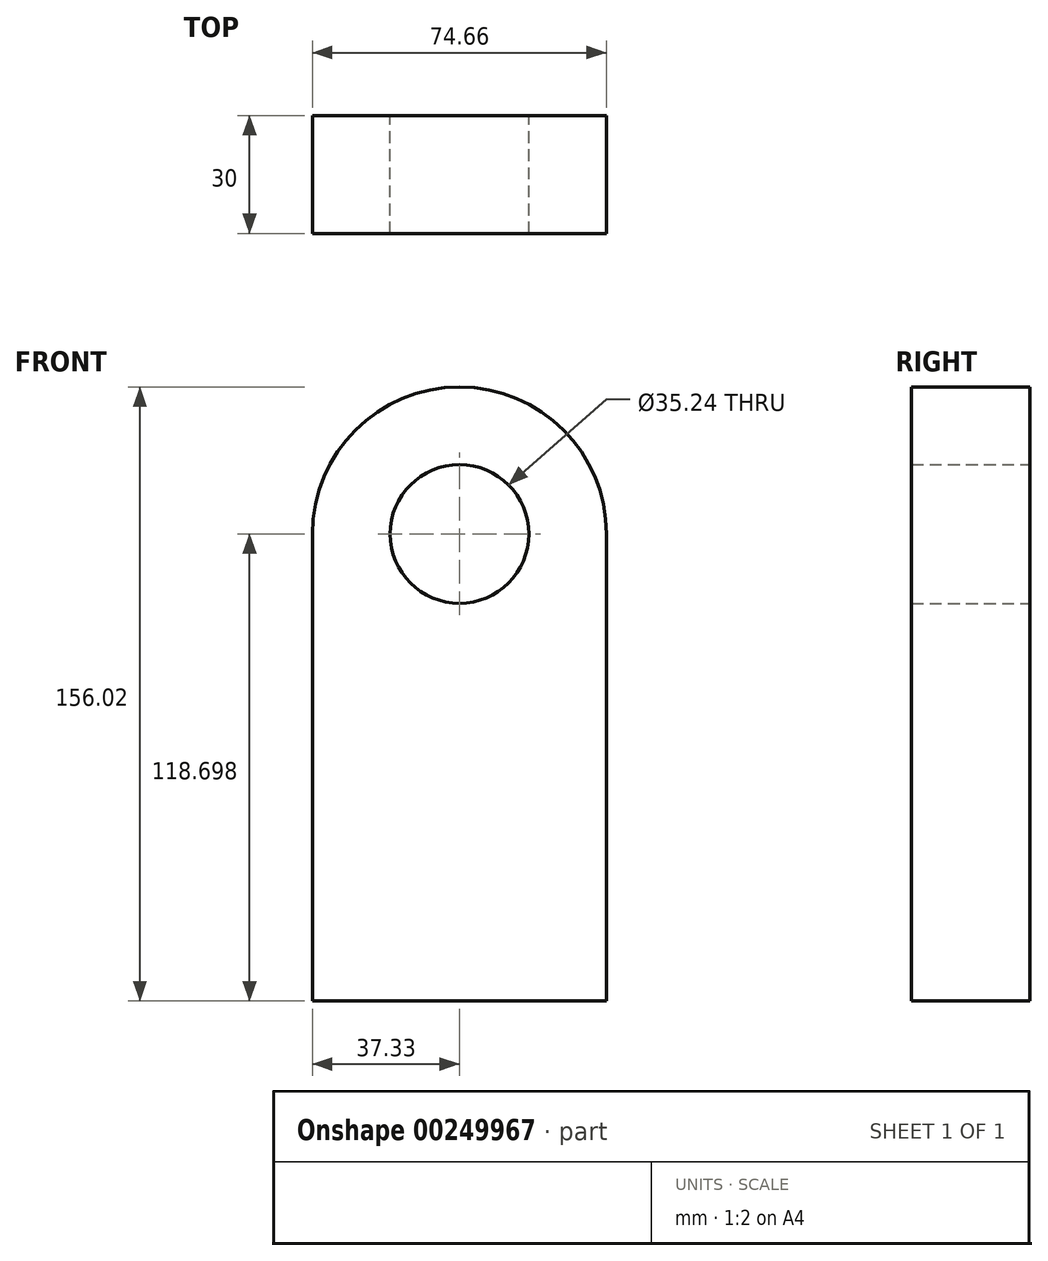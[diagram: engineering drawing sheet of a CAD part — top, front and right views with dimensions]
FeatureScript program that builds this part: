
annotation { "Feature Type Name" : "Feature", "Feature Type Description" : "" }
export const myFeature = defineFeature(function(context is Context, id is Id, definition is map)
    precondition{}
    {
        {
            var Q0;
            Q0=qCreatedBy(makeId("Front.planeOp"),FACE);
            var sketch = newSketch(context, id + "F0", { "sketchPlane" : qUnion([Q0])});
            skLineSegment(sketch, "E0.top", {"start": v(37.33, -59.35) * mm, "end": v(-37.33, -59.35) * mm});
            skLineSegment(sketch, "E0.left", {"start": v(37.33, 59.35) * mm, "end": v(37.33, -59.35) * mm});
            skLineSegment(sketch, "E0.right", {"start": v(-37.33, 59.35) * mm, "end": v(-37.33, -59.35) * mm});
            skPoint(sketch, "E0.middle", {"position": v(0, 0) * mm});
            skArc(sketch, "E1", {"start": v(37.33, 59.35) * mm, "mid": v(0, 96.67) * mm, "end": v(-37.33, 59.35) * mm});
            skCircle(sketch, "E2", {"center": v(0, 59.35) * mm, "radius": 17.62 * mm});
            skSolve(sketch);
        }
        {
            var Q0;
            Q0=makeQuery(id+"F0.imprint","IMPRINT",FACE,{"disambiguationData":[TD([[makeQuery(id+"F0.imprint","IMPRINT",EDGE,{"derivedFrom":sQuery(id+"F0.wireOp",EDGE,"E0.top")}),-1.0]])]});
            extrude(context, id + "F1", {"entities" : qUnion([Q0]), "depth" : 30 * mm});
        }
    });
